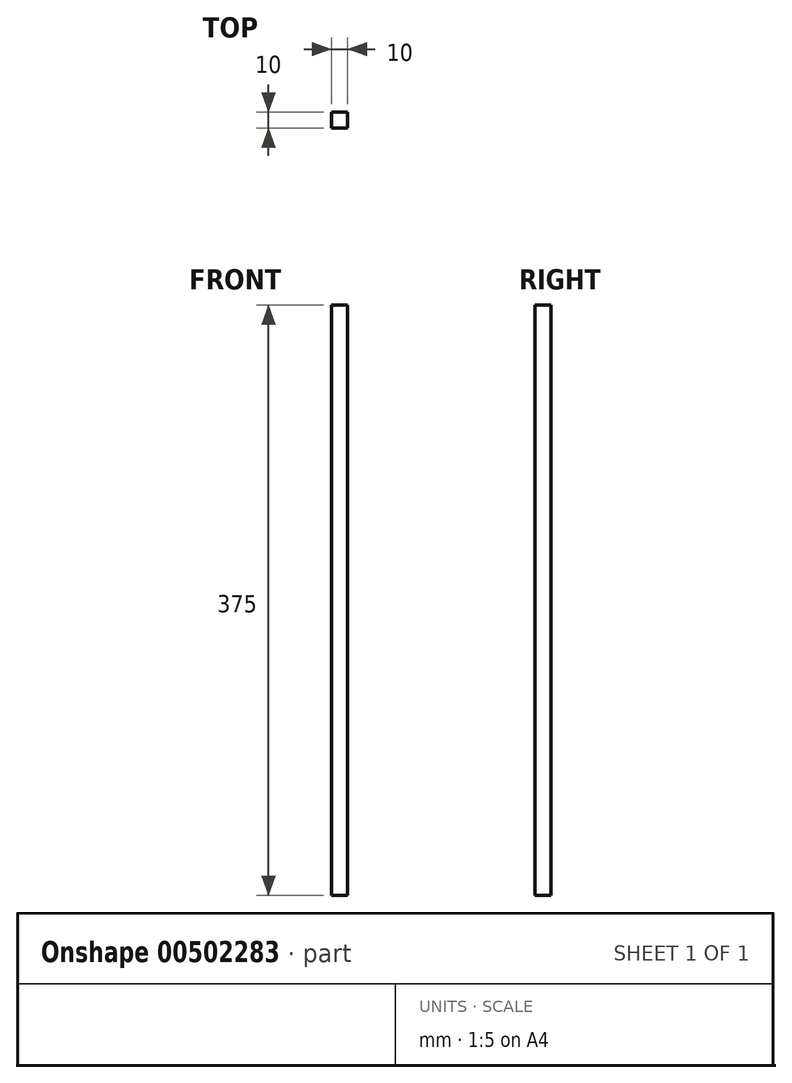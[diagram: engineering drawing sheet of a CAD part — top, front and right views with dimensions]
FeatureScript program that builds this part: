
annotation { "Feature Type Name" : "Feature", "Feature Type Description" : "" }
export const myFeature = defineFeature(function(context is Context, id is Id, definition is map)
    precondition{}
    {
        {
            var Q0;
            Q0=qCreatedBy(makeId("Top.planeOp"),FACE);
            var sketch = newSketch(context, id + "F0", { "sketchPlane" : qUnion([Q0])});
            skLineSegment(sketch, "E0.bottom", {"start": v(-5.93, 4.56) * mm, "end": v(4.07, 4.56) * mm});
            skLineSegment(sketch, "E0.top", {"start": v(-5.93, -5.44) * mm, "end": v(4.07, -5.44) * mm});
            skLineSegment(sketch, "E0.left", {"start": v(-5.93, 4.56) * mm, "end": v(-5.93, -5.44) * mm});
            skLineSegment(sketch, "E0.right", {"start": v(4.07, 4.56) * mm, "end": v(4.07, -5.44) * mm});
            skSolve(sketch);
        }
        {
            var Q0;
            Q0 = qSketchRegion(id + "F0", true);
            extrude(context, id + "F1", {"entities" : qUnion([Q0]), "depth" : 375 * mm});
        }
    });
